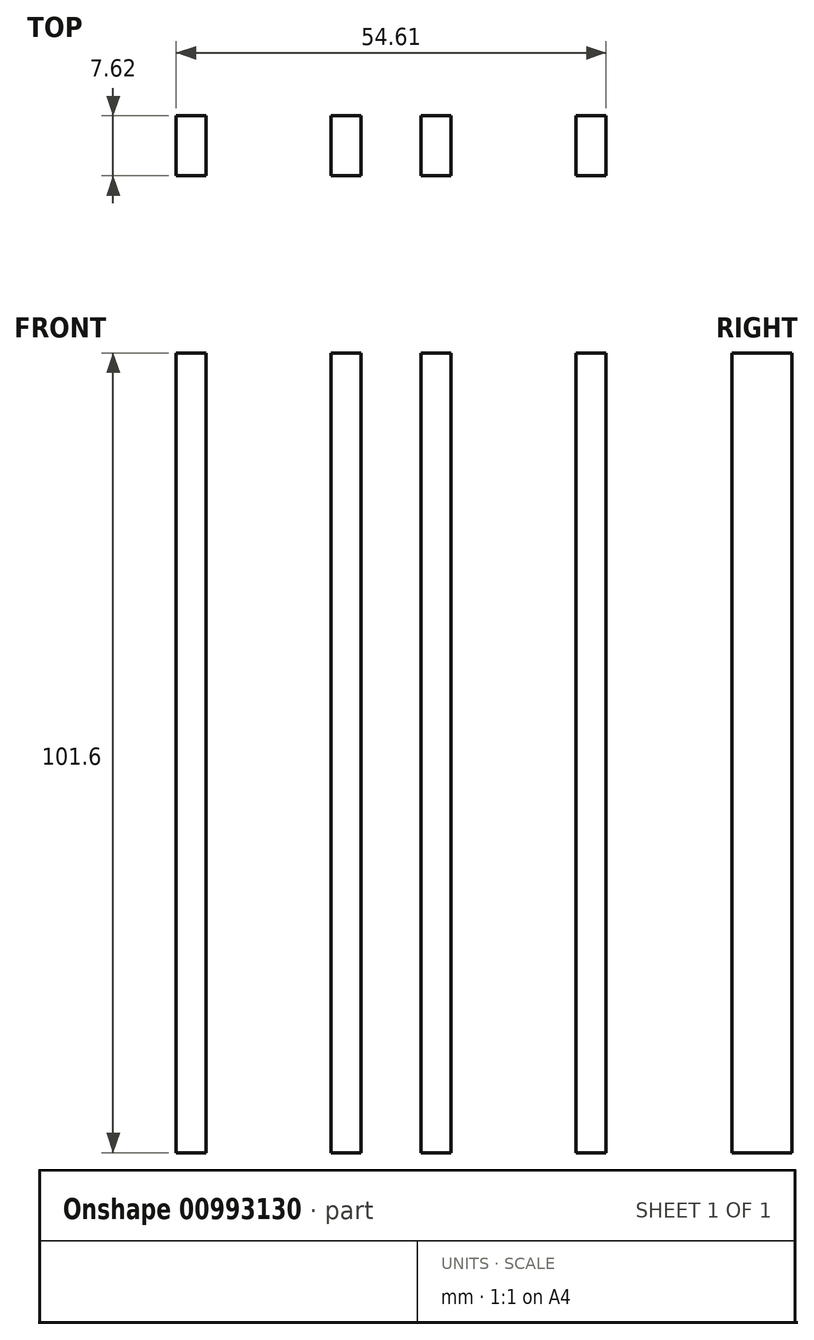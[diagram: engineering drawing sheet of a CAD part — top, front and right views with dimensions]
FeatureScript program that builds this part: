
annotation { "Feature Type Name" : "Feature", "Feature Type Description" : "" }
export const myFeature = defineFeature(function(context is Context, id is Id, definition is map)
    precondition{}
    {
        {
            var Q0;
            Q0=qCreatedBy(makeId("Front.planeOp"),FACE);
            var sketch = newSketch(context, id + "F0", { "sketchPlane" : qUnion([Q0])});
            skLineSegment(sketch, "E0.bottom", {"start": v(-80.26, 0.33) * mm, "end": v(-25.65, 0.33) * mm});
            skLineSegment(sketch, "E0.top", {"start": v(-80.26, -101.27) * mm, "end": v(-25.65, -101.27) * mm});
            skLineSegment(sketch, "E0.left", {"start": v(-80.26, 0.33) * mm, "end": v(-80.26, -101.27) * mm});
            skLineSegment(sketch, "E0.right", {"start": v(-25.65, 0.33) * mm, "end": v(-25.65, -101.27) * mm});
            skLineSegment(sketch, "E1.bottom", {"start": v(-49.15, 0.33) * mm, "end": v(-56.77, 0.33) * mm});
            skLineSegment(sketch, "E1.top", {"start": v(-49.15, -101.27) * mm, "end": v(-56.77, -101.27) * mm});
            skLineSegment(sketch, "E1.left", {"start": v(-49.15, 0.33) * mm, "end": v(-49.15, -101.27) * mm});
            skLineSegment(sketch, "E1.right", {"start": v(-56.77, 0.33) * mm, "end": v(-56.77, -101.27) * mm});
            skPoint(sketch, "E1.middle", {"position": v(-52.96, -50.47) * mm});
            skPoint(sketch, "E1.middle.positionSnap0", {"position": v(-52.96, 0.33) * mm});
            skPoint(sketch, "E1.centerSnap0", {"position": v(-52.96, 0.33) * mm});
            skLineSegment(sketch, "E2.bottom", {"start": v(-76.45, 0.33) * mm, "end": v(-60.58, 0.33) * mm});
            skLineSegment(sketch, "E2.top", {"start": v(-76.45, -101.27) * mm, "end": v(-60.58, -101.27) * mm});
            skLineSegment(sketch, "E2.left", {"start": v(-76.45, 0.33) * mm, "end": v(-76.45, -101.27) * mm});
            skLineSegment(sketch, "E2.right", {"start": v(-60.58, 0.33) * mm, "end": v(-60.58, -101.27) * mm});
            skLineSegment(sketch, "E3.bottom", {"start": v(-45.34, 0.33) * mm, "end": v(-29.46, 0.33) * mm});
            skLineSegment(sketch, "E3.top", {"start": v(-45.34, -101.27) * mm, "end": v(-29.46, -101.27) * mm});
            skLineSegment(sketch, "E3.left", {"start": v(-45.34, 0.33) * mm, "end": v(-45.34, -101.27) * mm});
            skLineSegment(sketch, "E3.right", {"start": v(-29.46, 0.33) * mm, "end": v(-29.46, -101.27) * mm});
            skLineSegment(sketch, "E4", {"start": v(-52.96, -4.75) * mm, "end": v(-49.15, 0.33) * mm});
            skLineSegment(sketch, "E5", {"start": v(-56.77, 0.33) * mm, "end": v(-52.96, -4.75) * mm});
            skSolve(sketch);
        }
        {
            var Q0;
            Q0=makeQuery(id+"F0.imprint","IMPRINT",FACE,{"disambiguationData":[TD([[makeQuery(id+"F0.imprint","IMPRINT",EDGE,{"derivedFrom":sQuery(id+"F0.wireOp",EDGE,"E2.bottom")}),-1.0]])]});
            var Q1;
            Q1=makeQuery(id+"F0.imprint","IMPRINT",FACE,{"disambiguationData":[TD([[makeQuery(id+"F0.imprint","IMPRINT",EDGE,{"derivedFrom":sQuery(id+"F0.wireOp",EDGE,"E3.bottom")}),-1.0]])]});
            var Q2;
            {var subQ0=sQuery(id+"F0.wireOp",EDGE,"E1.right");Q2=makeQuery(id+"F0.imprint","IMPRINT",FACE,{"disambiguationData":[TD([[makeQuery(id+"F0.imprint","IMPRINT",EDGE,{"derivedFrom":subQ0}),-1.0]])]});}
            var Q3;
            {var subQ0=sQuery(id+"F0.wireOp",EDGE,"E1.left");Q3=makeQuery(id+"F0.imprint","IMPRINT",FACE,{"disambiguationData":[TD([[makeQuery(id+"F0.imprint","IMPRINT",EDGE,{"derivedFrom":subQ0}),1.0]])]});}
            var Q4;
            {var subQ0=sQuery(id+"F0.wireOp",EDGE,"E0.right");Q4=makeQuery(id+"F0.imprint","IMPRINT",FACE,{"disambiguationData":[TD([[makeQuery(id+"F0.imprint","IMPRINT",EDGE,{"derivedFrom":subQ0}),-1.0]])]});}
            var Q5;
            {var subQ0=sQuery(id+"F0.wireOp",EDGE,"E0.left");Q5=makeQuery(id+"F0.imprint","IMPRINT",FACE,{"disambiguationData":[TD([[makeQuery(id+"F0.imprint","IMPRINT",EDGE,{"derivedFrom":subQ0}),1.0]])]});}
            var Q6;
            Q6=makeQuery(id+"F0.imprint","IMPRINT",FACE,{"disambiguationData":[TD([[makeQuery(id+"F0.imprint","IMPRINT",EDGE,{"derivedFrom":sQuery(id+"F0.wireOp",EDGE,"E1.top")}),-1.0]])]});
            extrude(context, id + "F1", {"entities" : qUnion([Q0, Q1, Q2, Q3, Q4, Q5, Q6]), "depth" : 3.8 * mm, "offsetDistance" : 25.4 * mm});
        }
        {
            var Q0;
            {var subQ0=sQuery(id+"F0.wireOp",EDGE,"E1.right");Q0=makeQuery(id+"F0.imprint","IMPRINT",FACE,{"disambiguationData":[TD([[makeQuery(id+"F0.imprint","IMPRINT",EDGE,{"derivedFrom":subQ0}),-1.0]])]});}
            var Q1;
            {var subQ0=sQuery(id+"F0.wireOp",EDGE,"E1.left");Q1=makeQuery(id+"F0.imprint","IMPRINT",FACE,{"disambiguationData":[TD([[makeQuery(id+"F0.imprint","IMPRINT",EDGE,{"derivedFrom":subQ0}),1.0]])]});}
            var Q2;
            {var subQ0=sQuery(id+"F0.wireOp",EDGE,"E0.right");Q2=makeQuery(id+"F0.imprint","IMPRINT",FACE,{"disambiguationData":[TD([[makeQuery(id+"F0.imprint","IMPRINT",EDGE,{"derivedFrom":subQ0}),-1.0]])]});}
            var Q3;
            {var subQ0=sQuery(id+"F0.wireOp",EDGE,"E0.left");Q3=makeQuery(id+"F0.imprint","IMPRINT",FACE,{"disambiguationData":[TD([[makeQuery(id+"F0.imprint","IMPRINT",EDGE,{"derivedFrom":subQ0}),1.0]])]});}
            extrude(context, id + "F2", {"entities" : qUnion([Q0, Q1, Q2, Q3]), "operationType" : NewBodyOperationType.ADD, "oppositeDirection" : true, "depth" : 3.8 * mm, "offsetDistance" : 25.4 * mm});
        }
    });
